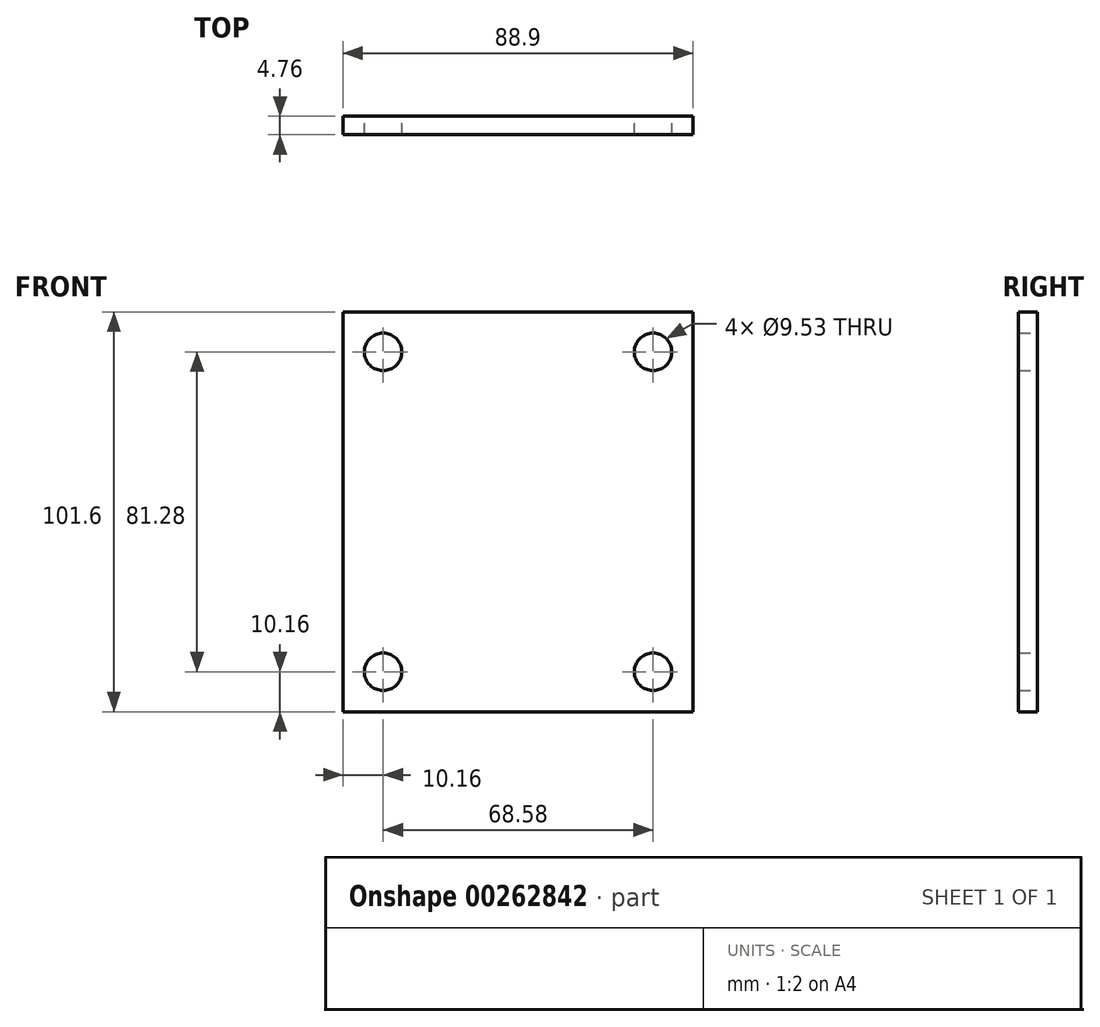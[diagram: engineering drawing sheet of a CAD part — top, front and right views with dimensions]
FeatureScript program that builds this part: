
annotation { "Feature Type Name" : "Feature", "Feature Type Description" : "" }
export const myFeature = defineFeature(function(context is Context, id is Id, definition is map)
    precondition{}
    {
        {
            var Q0;
            Q0=qCreatedBy(makeId("Front.planeOp"),FACE);
            var sketch = newSketch(context, id + "F0", { "sketchPlane" : qUnion([Q0])});
            skLineSegment(sketch, "E0.bottom", {"start": v(44.45, -50.8) * mm, "end": v(-44.45, -50.8) * mm});
            skLineSegment(sketch, "E0.top", {"start": v(44.45, 50.8) * mm, "end": v(-44.45, 50.8) * mm});
            skLineSegment(sketch, "E0.left", {"start": v(44.45, -50.8) * mm, "end": v(44.45, 50.8) * mm});
            skLineSegment(sketch, "E0.right", {"start": v(-44.45, -50.8) * mm, "end": v(-44.45, 50.8) * mm});
            skPoint(sketch, "E0.middle", {"position": v(0, 0) * mm});
            skCircle(sketch, "E1", {"center": v(-34.3, 40.64) * mm, "radius": 4.76 * mm});
            skCircle(sketch, "E2.MirrorC", {"center": v(34.3, 40.64) * mm, "radius": 4.76 * mm});
            skCircle(sketch, "E3.MirrorC", {"center": v(34.3, -40.64) * mm, "radius": 4.76 * mm});
            skCircle(sketch, "E4.MirrorC", {"center": v(-34.3, -40.64) * mm, "radius": 4.76 * mm});
            skSolve(sketch);
        }
        {
            var Q0;
            Q0 = qSketchRegion(id + "F0", true);
            extrude(context, id + "F1", {"entities" : qUnion([Q0]), "depth" : 4.76 * mm});
        }
    });
